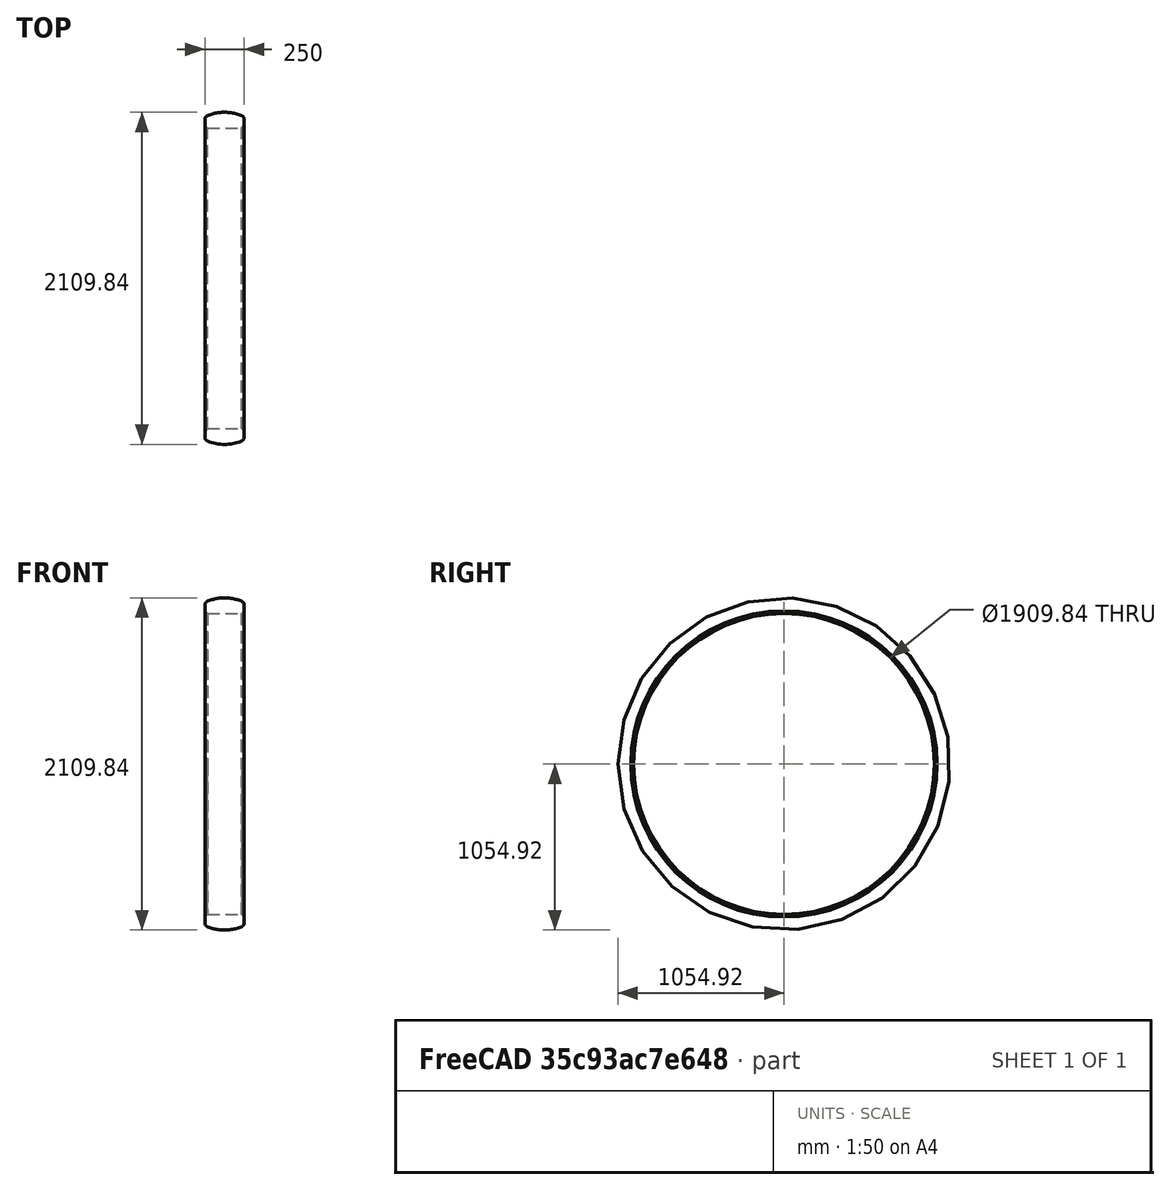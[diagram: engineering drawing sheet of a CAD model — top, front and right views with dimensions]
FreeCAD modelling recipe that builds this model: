
FCSTD DOCUMENT
Label: zipfile_write
objects: Sketcher::SketchObject×1, PartDesign::Revolution×1
note: 3 computed .brp shape members not serialized (recipe doc carries the construction recipe); baked Part::Feature solids carry a one-line shape summary decoded from their .brp

FEATURE [Sketcher::SketchObject] Sketch
  sketch-geometry (9):
    g0: LineSegment StartX=17.6777 StartY=-954.92 StartZ=0 EndX=232.322 EndY=-954.92 EndZ=0
    g1: LineSegment StartX=0 StartY=-972.598 StartZ=0 EndX=0 EndY=-1008.23 EndZ=0
    g2: LineSegment StartX=17.6777 StartY=-954.92 StartZ=0 EndX=0 EndY=-972.598 EndZ=0
    g3: LineSegment StartX=232.322 StartY=-954.92 StartZ=0 EndX=250 EndY=-972.598 EndZ=0
    g4: LineSegment StartX=250 StartY=-1008.23 StartZ=0 EndX=250 EndY=-972.598 EndZ=0
    g5: ArcOfCircle CenterX=28 CenterY=-1008.23 CenterZ=0 NormalX=0 NormalY=0 NormalZ=1 Radius=28 StartAngle=3.14159 EndAngle=4.33161
    g6: ArcOfCircle CenterX=222 CenterY=-1008.23 CenterZ=0 NormalX=0 NormalY=0 NormalZ=1 Radius=28 StartAngle=5.09317 EndAngle=6.28319
    g7: ArcOfCircle CenterX=125 CenterY=-765.92 CenterZ=0 NormalX=0 NormalY=0 NormalZ=1 Radius=289 StartAngle=4.33161 EndAngle=5.09317
    g8: LineSegment [constr] StartX=21.3562 StartY=-1054.92 StartZ=0 EndX=437.798 EndY=-1054.92 EndZ=0
  constraints (27):
    c: Horizontal(g0)
    c: DistanceY(g0) = -954.92
    c: Vertical(g1)
    c: Coincident(g2,g0)
    c: Coincident(g2,g1)
    c: Coincident(g3,g0)
    c: Vertical(g4)
    c: Coincident(g3,g4)
    c: DistanceX(g1) = 0
    c: Angle(g1,g2) = 2.35619
    c: Angle(g3,g4) = 2.35619
    c: DistanceX(g1,g3) = 6000
    c: Distance(g2) = 60
    c: Distance(g3) = 60
    c: Radius(g5) = 100
    c: Radius(g6) = 100
    c: Radius(g7) = 522
    c: Tangent(g1,g5)
    c: Tangent(g5,g7)
    c: Tangent(g7,g6)
    c: Tangent(g6,g4)
    c: Horizontal(g8)
    c: Tangent(g8,g7)
    c: DistanceY(g8,g0) = 310
    c: DistanceX(g7) = 300
    c: DistanceX(g8) = 21.3562
    c: Distance(g8) = 1.442
FEATURE [PartDesign::Revolution] Revolution
  Angle = 360
  Axis = (1,0,0)
  Base = (0,0,0)
  ReferenceAxis = -> Sketch [H_Axis]
  Sketch = -> Sketch
